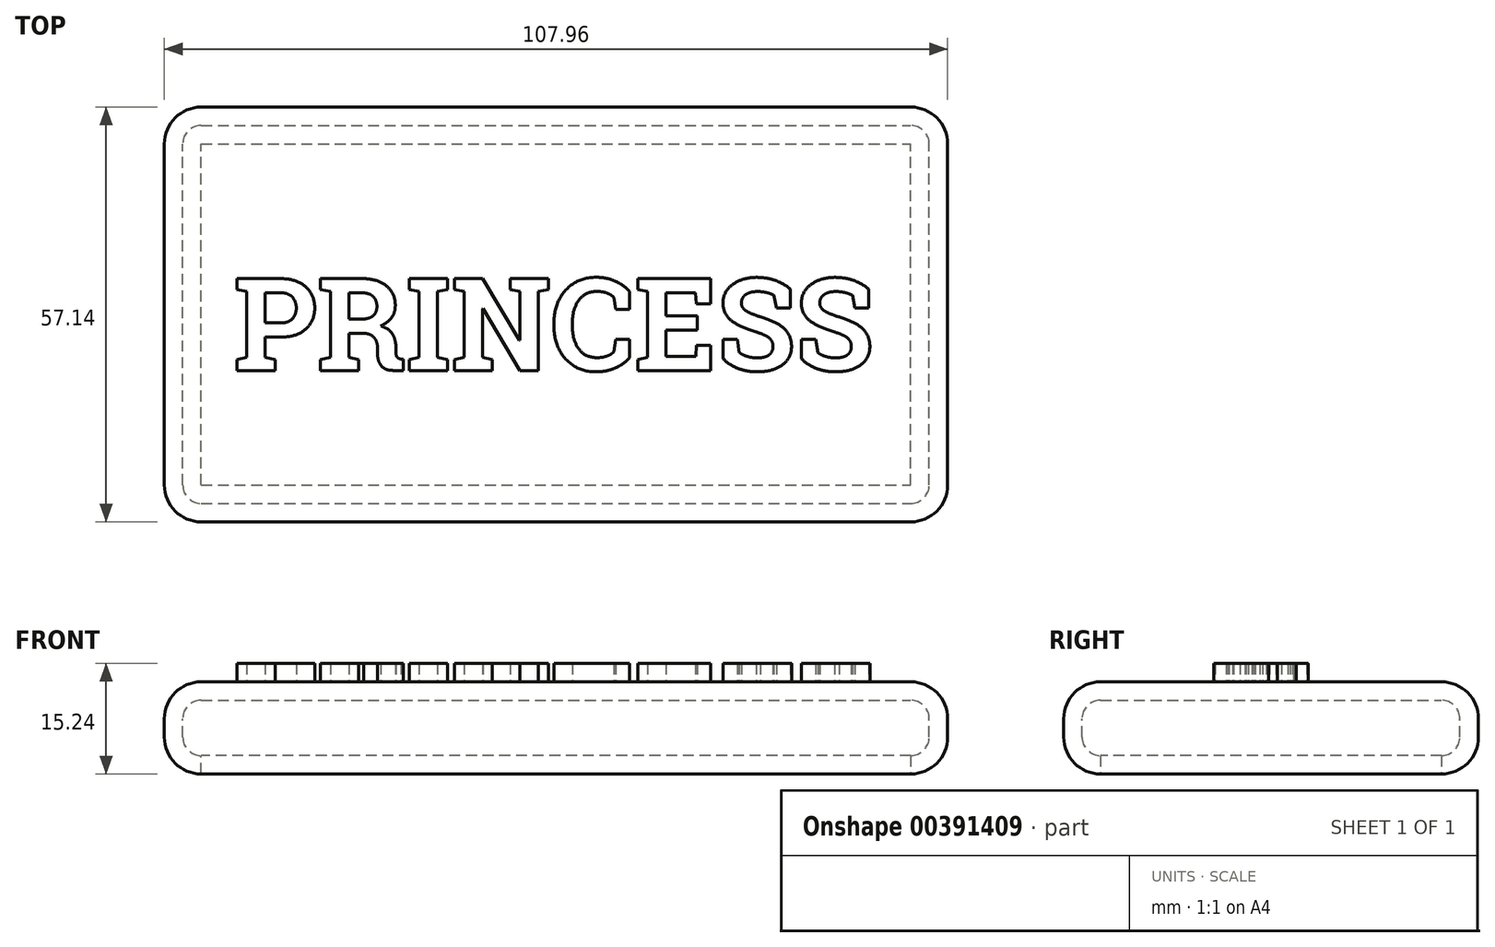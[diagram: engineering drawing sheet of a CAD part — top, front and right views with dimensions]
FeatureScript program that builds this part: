
annotation { "Feature Type Name" : "Feature", "Feature Type Description" : "" }
export const myFeature = defineFeature(function(context is Context, id is Id, definition is map)
    precondition{}
    {
        {
            var Q0;
            Q0=qCreatedBy(makeId("Top.planeOp"),FACE);
            var sketch = newSketch(context, id + "F0", { "sketchPlane" : qUnion([Q0])});
            skLineSegment(sketch, "E0.bottom", {"start": v(-53.97, -28.58) * mm, "end": v(53.98, -28.58) * mm});
            skLineSegment(sketch, "E0.top", {"start": v(-53.98, 28.58) * mm, "end": v(53.97, 28.58) * mm});
            skLineSegment(sketch, "E0.left", {"start": v(-53.97, -28.58) * mm, "end": v(-53.98, 28.58) * mm});
            skLineSegment(sketch, "E0.right", {"start": v(53.98, -28.58) * mm, "end": v(53.98, 28.58) * mm});
            skPoint(sketch, "E0.middle", {"position": v(0, 0) * mm});
            skSolve(sketch);
        }
        {
            var Q0;
            Q0=makeQuery(id+"F0.imprint","IMPRINT",FACE,{"disambiguationData":[TD([[makeQuery(id+"F0.imprint","IMPRINT",EDGE,{"derivedFrom":sQuery(id+"F0.wireOp",EDGE,"E0.bottom")}),1.0]])]});
            extrude(context, id + "F1", {"entities" : qUnion([Q0]), "depth" : 12.7 * mm});
        }
        {
            var Q0;
            Q0=makeQuery(id+"F1.opExtrude","CAP_FACE",FACE,{"disambiguationData":[OSD([sQuery(id+"F0.wireOp",EDGE,"E0.bottom"),sQuery(id+"F0.wireOp",EDGE,"E0.top"),sQuery(id+"F0.wireOp",EDGE,"E0.left"),sQuery(id+"F0.wireOp",EDGE,"E0.right")])],"isStart":false});
            var Q1;
            Q1=makeQuery(id+"F1.opExtrude","SWEPT_FACE",FACE,{"disambiguationData":[OSD([sQuery(id+"F0.wireOp",EDGE,"E0.top")])]});
            var Q2;
            Q2=makeQuery(id+"F1.opExtrude","SWEPT_FACE",FACE,{"disambiguationData":[OSD([sQuery(id+"F0.wireOp",EDGE,"E0.left")])]});
            var Q3;
            Q3=makeQuery(id+"F1.opExtrude","SWEPT_FACE",FACE,{"disambiguationData":[OSD([sQuery(id+"F0.wireOp",EDGE,"E0.right")])]});
            var Q4;
            Q4=makeQuery(id+"F1.opExtrude","SWEPT_FACE",FACE,{"disambiguationData":[OSD([sQuery(id+"F0.wireOp",EDGE,"E0.bottom")])]});
            fillet(context, id + "F2", {"entities" : qUnion([Q0, Q1, Q2, Q3, Q4]), "radius" : 5.08 * mm, "tangentPropagation" : true, "allowEdgeOverflow" : false});
        }
        {
            var Q0;
            Q0=makeQuery(id+"F1.opExtrude","CAP_FACE",FACE,{"disambiguationData":[OSD([sQuery(id+"F0.wireOp",EDGE,"E0.bottom"),sQuery(id+"F0.wireOp",EDGE,"E0.top"),sQuery(id+"F0.wireOp",EDGE,"E0.left"),sQuery(id+"F0.wireOp",EDGE,"E0.right")])],"isStart":true});
            shell(context, id + "F3", {"entities" : qUnion([Q0]), "thickness" : 2.54 * mm});
        }
        {
            var Q0;
            Q0=makeQuery(id+"F1.opExtrude","CAP_FACE",FACE,{"disambiguationData":[OSD([sQuery(id+"F0.wireOp",EDGE,"E0.bottom"),sQuery(id+"F0.wireOp",EDGE,"E0.top"),sQuery(id+"F0.wireOp",EDGE,"E0.left"),sQuery(id+"F0.wireOp",EDGE,"E0.right")])],"isStart":false});
            var sketch = newSketch(context, id + "F4", { "sketchPlane" : qUnion([Q0])});
            skText(sketch, "E1", { "text": "PRINCESS", "fontName": "RobotoSlab-Bold.ttf"});
            const initialGuessF4  = {"E1": [-0.04445, -0.00772, 1, 0, 0.01282]};
            skSetInitialGuess(sketch, initialGuessF4);
            skSolve(sketch);
        }
        {
            var Q0;
            Q0 = qSketchRegion(id + "F4", true);
            extrude(context, id + "F5", {"entities" : qUnion([Q0]), "operationType" : NewBodyOperationType.ADD, "depth" : 2.54 * mm});
        }
    });
